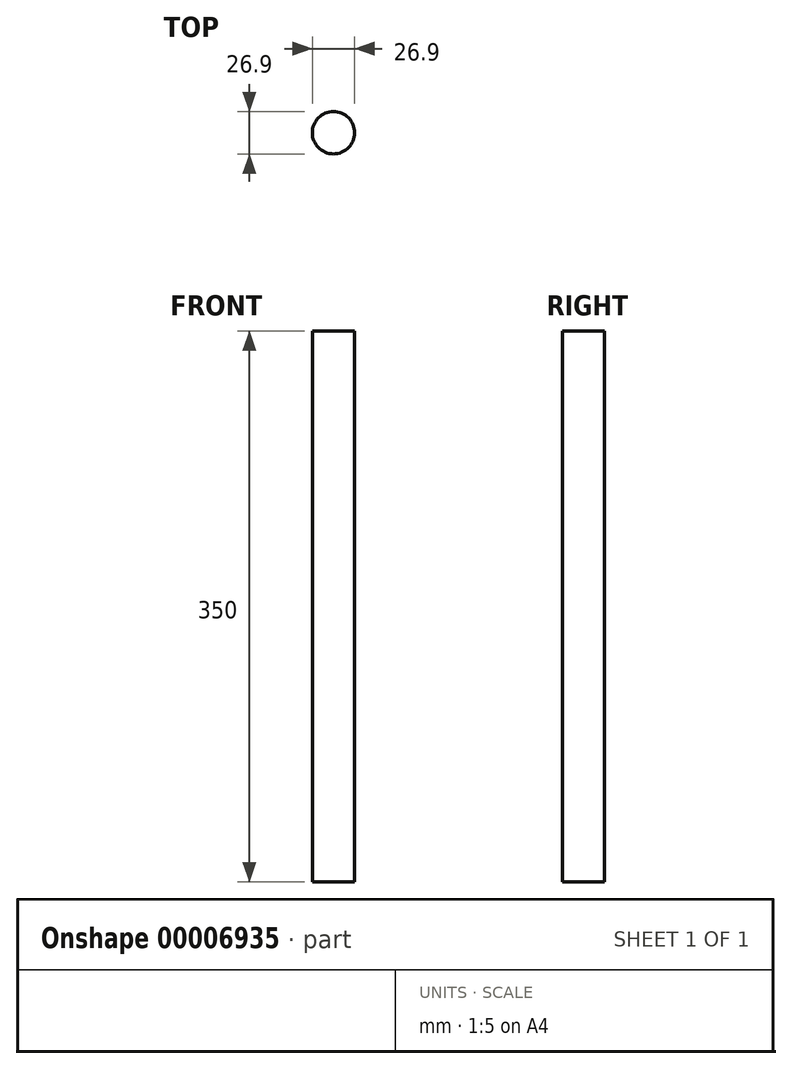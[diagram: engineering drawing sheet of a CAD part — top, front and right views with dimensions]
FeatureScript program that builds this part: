
annotation { "Feature Type Name" : "Feature", "Feature Type Description" : "" }
export const myFeature = defineFeature(function(context is Context, id is Id, definition is map)
    precondition{}
    {
        {
            var Q0;
            Q0=qCreatedBy(makeId("Top.planeOp"),FACE);
            var sketch = newSketch(context, id + "F0", { "sketchPlane" : qUnion([Q0])});
            skCircle(sketch, "E0", {"center": v(0, 0) * mm, "radius": 13.45 * mm});
            skSolve(sketch);
        }
        {
            var Q0;
            Q0=makeQuery(id+"F0.imprint","IMPRINT",FACE,{"disambiguationData":[TD([[makeQuery(id+"F0.imprint","IMPRINT",EDGE,{"derivedFrom":sQuery(id+"F0.wireOp",EDGE,"E0")}),1.0]])]});
            extrude(context, id + "F1", {"entities" : qUnion([Q0]), "depth" : (350) * mm});
        }
    });
